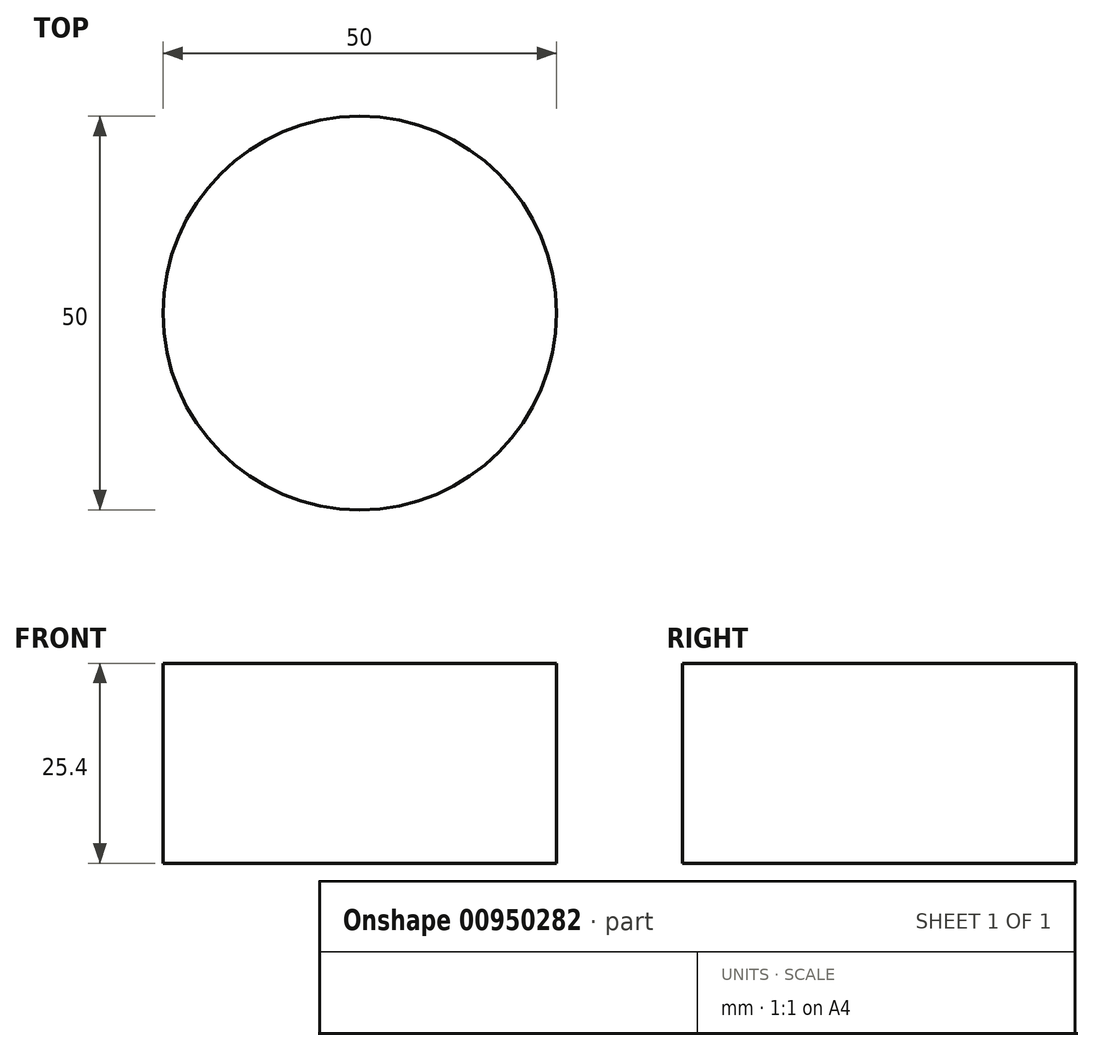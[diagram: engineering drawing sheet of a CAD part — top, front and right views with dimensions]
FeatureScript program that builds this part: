
annotation { "Feature Type Name" : "Feature", "Feature Type Description" : "" }
export const myFeature = defineFeature(function(context is Context, id is Id, definition is map)
    precondition{}
    {
        {
            var Q0;
            Q0=qCreatedBy(makeId("Top.planeOp"),FACE);
            var sketch = newSketch(context, id + "F0", { "sketchPlane" : qUnion([Q0])});
            skCircle(sketch, "E0", {"center": v(0, 0) * mm, "radius": 25 * mm});
            skSolve(sketch);
        }
        {
            var Q0;
            Q0=makeQuery(id+"F0.imprint","IMPRINT",FACE,{"disambiguationData":[TD([[makeQuery(id+"F0.imprint","IMPRINT",EDGE,{"derivedFrom":sQuery(id+"F0.wireOp",EDGE,"E0")}),1.0]])]});
            extrude(context, id + "F1", {"entities" : qUnion([Q0]), "depth" : 25.4 * mm, "offsetDistance" : 25.4 * mm});
        }
    });
